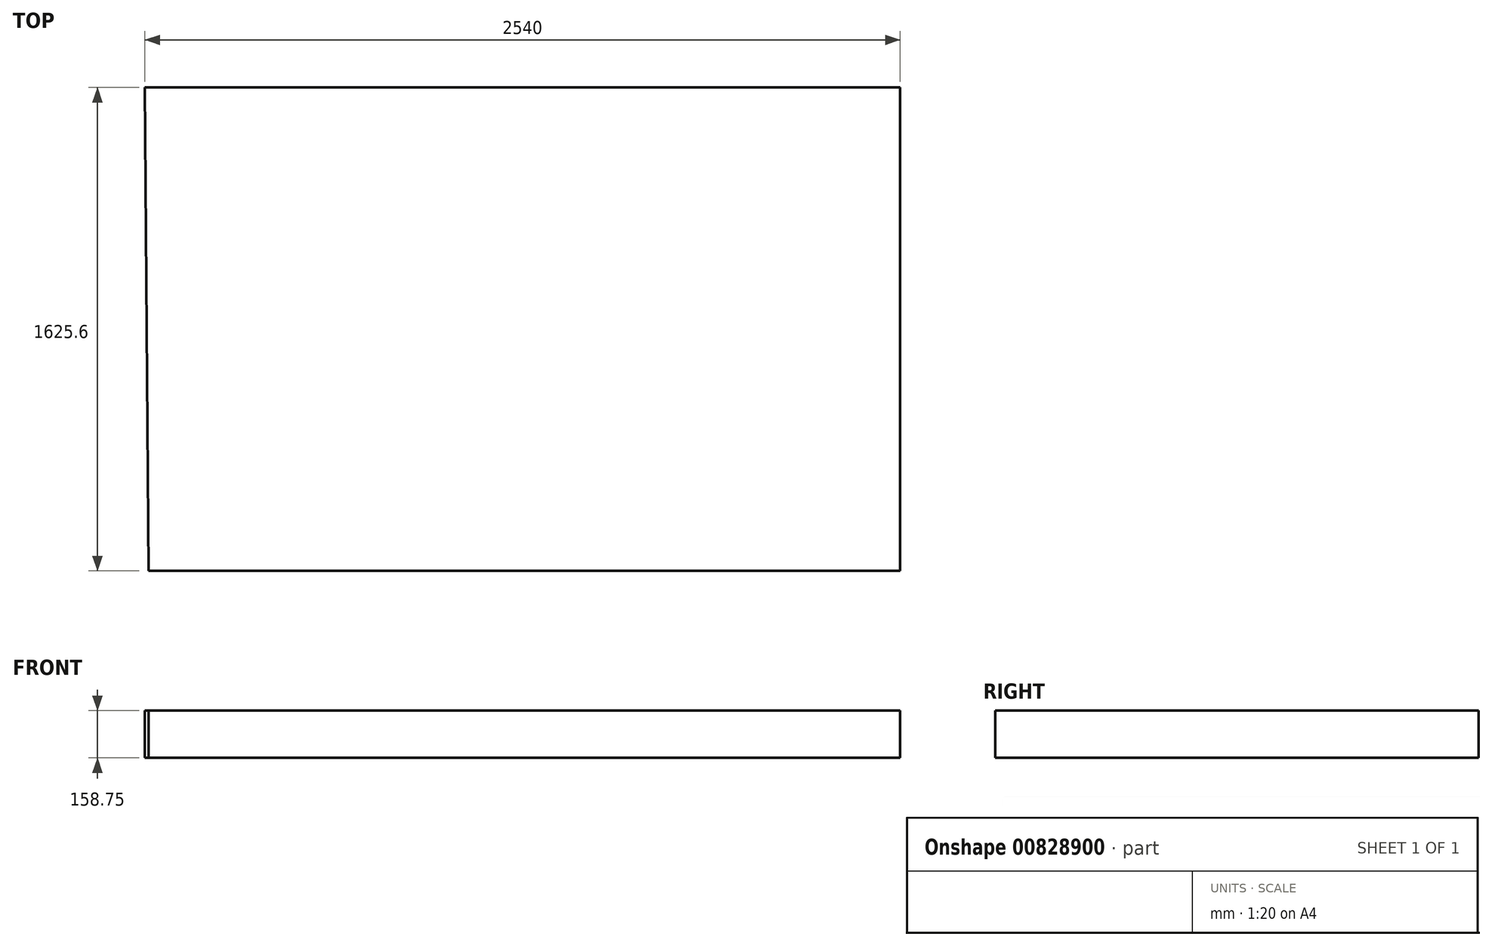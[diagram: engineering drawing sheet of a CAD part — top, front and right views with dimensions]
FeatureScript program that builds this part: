
annotation { "Feature Type Name" : "Feature", "Feature Type Description" : "" }
export const myFeature = defineFeature(function(context is Context, id is Id, definition is map)
    precondition{}
    {
        {
            var Q0;
            Q0=qCreatedBy(makeId("Top.planeOp"),FACE);
            var sketch = newSketch(context, id + "F0", { "sketchPlane" : qUnion([Q0])});
            skLineSegment(sketch, "E0", {"start": v(0, 0) * mm, "end": v(2527.3, 0) * mm});
            skLineSegment(sketch, "E1", {"start": v(2527.3, 0) * mm, "end": v(2527.3, 1625.6) * mm});
            skLineSegment(sketch, "E2", {"start": v(2527.3, 1625.6) * mm, "end": v(-12.7, 1625.6) * mm});
            skLineSegment(sketch, "E3", {"start": v(-12.7, 1625.6) * mm, "end": v(0, 0) * mm});
            skSolve(sketch);
        }
        {
            var Q0;
            Q0=makeQuery(id+"F0.imprint","IMPRINT",FACE,{"disambiguationData":[TD([[makeQuery(id+"F0.imprint","IMPRINT",EDGE,{"derivedFrom":sQuery(id+"F0.wireOp",EDGE,"E0")}),1.0]])]});
            extrude(context, id + "F1", {"entities" : qUnion([Q0]), "depth" : 158.75 * mm, "offsetDistance" : 25.4 * mm});
        }
    });
